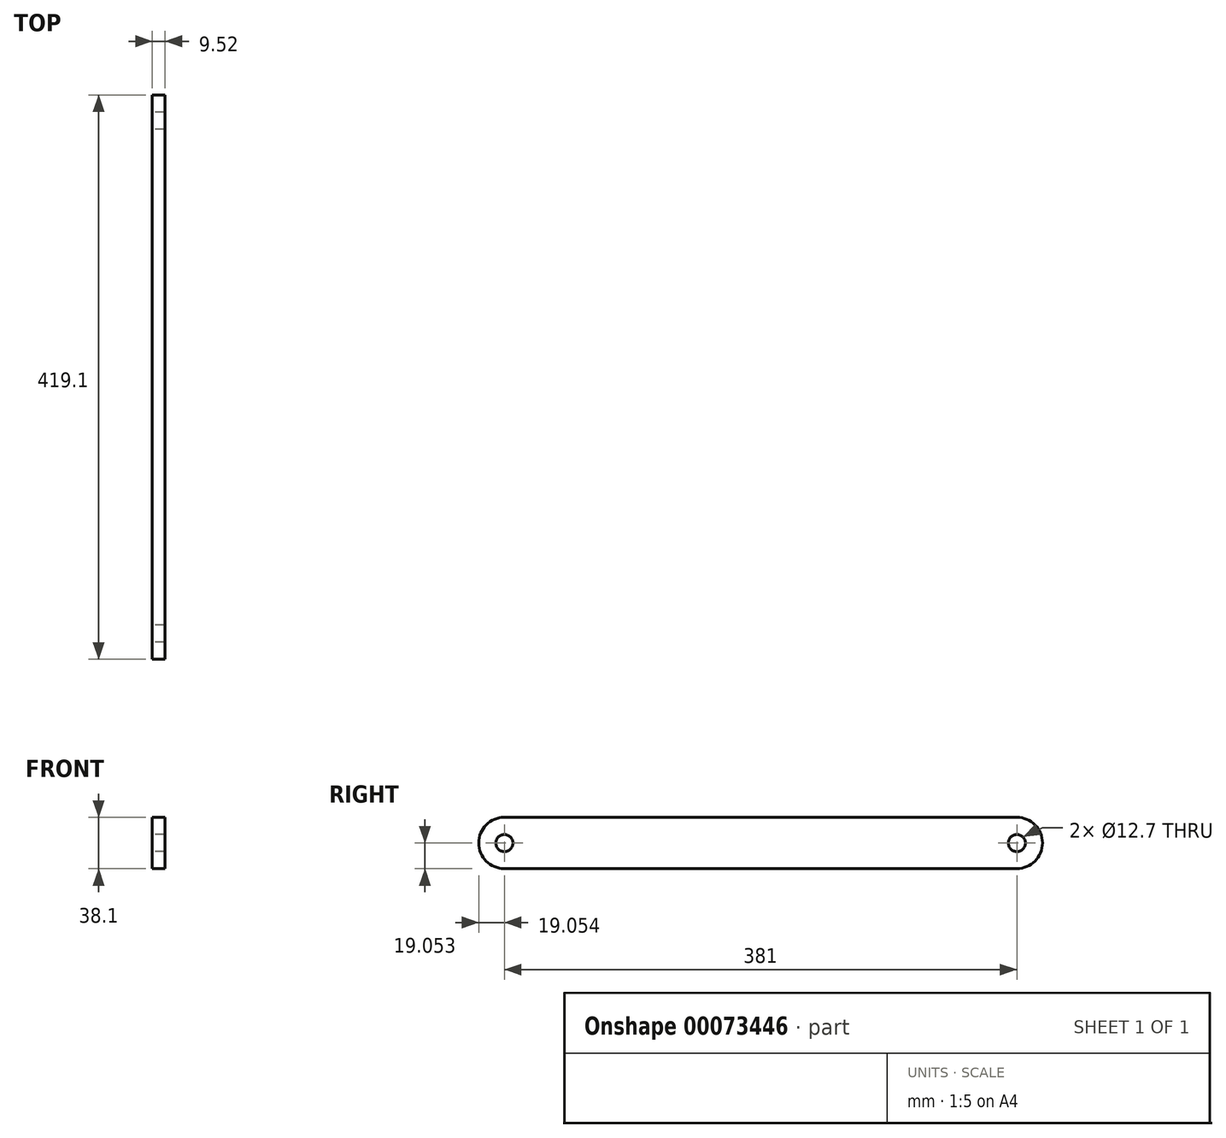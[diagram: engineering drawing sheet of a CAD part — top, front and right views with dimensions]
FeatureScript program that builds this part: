
annotation { "Feature Type Name" : "Feature", "Feature Type Description" : "" }
export const myFeature = defineFeature(function(context is Context, id is Id, definition is map)
    precondition{}
    {
        {
            var Q0;
            Q0=qCreatedBy(makeId("Right.planeOp"),FACE);
            var sketch = newSketch(context, id + "F0", { "sketchPlane" : qUnion([Q0])});
            skLineSegment(sketch, "E0", {"start": v(163.55, -20.82) * mm, "end": v(-217.45, -20.82) * mm});
            skArc(sketch, "E1", {"start": v(-217.45, -20.82) * mm, "mid": v(-236.5, -1.77) * mm, "end": v(-217.45, 17.28) * mm});
            skLineSegment(sketch, "E2", {"start": v(-217.45, 17.28) * mm, "end": v(163.55, 17.28) * mm});
            skArc(sketch, "E3", {"start": v(163.55, 17.28) * mm, "mid": v(182.6, -1.77) * mm, "end": v(163.55, -20.82) * mm});
            skCircle(sketch, "E4", {"center": v(-217.45, -1.77) * mm, "radius": 6.35 * mm});
            skCircle(sketch, "E5", {"center": v(163.55, -1.77) * mm, "radius": 6.35 * mm});
            skSolve(sketch);
        }
        {
            var Q0;
            Q0 = qSketchRegion(id + "F0", true);
            extrude(context, id + "F1", {"entities" : qUnion([Q0]), "endBound" : BoundingType.SYMMETRIC, "depth" : 9.52 * mm});
        }
    });
